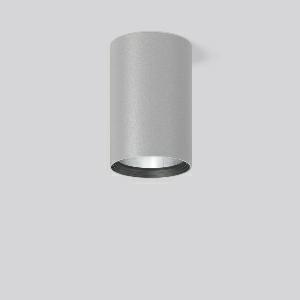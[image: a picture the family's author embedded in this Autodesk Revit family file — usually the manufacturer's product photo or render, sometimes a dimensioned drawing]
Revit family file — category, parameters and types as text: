
# Revit family: heledon_maxi_a_931217_004_1_d313
name_source: partatom
category: Lighting Fixtures
units: mm (PartAtom-declared; Revit-internal decimal feet)

## family parameters
Cut with Voids When Loaded = No
Host = Face
Light Source = No
Part Type = Normal
Room Calculation Point = No
Round Connector Dimension = Use Diameter
Shared = No

## types (1)
- HELEDON maxi A (1 x LED Modul 940, 3500 lm, 4000)
    Apparent Load = 25 VA
    Approval mark = CE
    CIE Flux Codes = 100 100 100 100 100
    Color Rendering = 92
    Color Temperature = 4000
    Default Elevation = 1800 mm
    Description = Series: HELEDON maxi
Cylindrical surface-mounted downlight. Housing: die-cast aluminium, powder-coated. Internal ceiling frame polycarbonate with bayonet mounting. Black plastic ring and recessed LED to prevent glare from the side. Optical assembly with reflector made of MIRO-Silver with 98% total light reflection for outstanding efficiency - can be changed without tools. Best colour rendering index Ra>90. Suitable for Ceiling mounting. Easy installation with a separate ceiling frame with bayonet mounting and plug connection. Driver integrated. Connected via plug-in connector. High quality converter without flickering and stroboscopic effect. The following accessories can be mounted without use of tools: interchangeable lenses, decorative glasses, honeycomb louvre, clear and frosted diffusers, white interchangeable plastic ring. 
Colour: silver
Diameter: 123 mm
Height: 183 mm
Lamp: LED
Socket: without socket
Colour temperature: 4000K
Colour rendering index (CRI): 92
System power: 25 W
Rated luminous flux: 3500 lm
Luminous efficiency: 140 lm/W
Control gear: Regulated power supply
Protection class: I
Type of protection: IP 20
    Height = 183 mm
    Lamp = 1 x LED Modul 940
    Lamp Light Flux = 3500 lm
    Lamp count = 1
    Length = 123 mm
    Lifetime = 50000 h
    Luminous efficacy = 140 lm/W
    Manufacturer = RZB
    ModVariant = No
    Model = 931217.004.1
    Mounting Place = Ceiling
    Mounting Type = Surface mounted
    Number of Poles = 1
    OnlyDefault = Yes
    Power Factor = 1
    Product Name = HELEDON maxi A
    Product group = Surface mounted downlights
    ProductGroupID = 302
    Protection Class = Protection class I
    Protection Degree = IP 20
    RLX_Detail_Level = 1
    RLX_Emergency_Light_Flux = 0 lm
    RLX_Emergency_Type = 0
    RLX_Emergency_Type_DB = No
    RlxData = <blob elided: 98649 chars, md5=9f80a1c6>
    Socket = socket
    Standby Power = 0 W
    System Light Flux = 3500 lm
    System Power = 25 W
    Type Comments = Product without accessories
    Type Image = 931192.004.jpg
    URL = http://relux.com
    VarID = ---
    Voltage = 230 V
    Voltage Range = 220-240 V
    Weight = 0.00 kg
    Width = 0 mm  [stored 0 ft]

note: [stored X ft] marks values corroborated as IEEE doubles in the binary element streams (Revit-internal decimal feet)

## geometry (parser evidence)
native form markers: Blend x4, Sweep x10
no freeform markers — native parametric forms only
